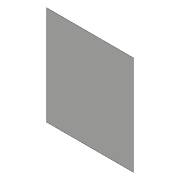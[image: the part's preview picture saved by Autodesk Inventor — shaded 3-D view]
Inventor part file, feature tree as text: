
AUTODESK INVENTOR PART (.ipt)
format: ipt  version: 2017 (Build 210142000, 142)  size: 75,264 bytes
history: native  units: mm
features: extrude x1, sketch x1
ambient origin geometry x8: Origin, YZ Plane, XZ Plane, XY Plane, X Axis, Y Axis, Z Axis, Center Point
bodies: Body1 (feature_tree)
feature tree (2):
  extrude  "Extrusion1"  Depth=838.2mm
  sketch  "Sketch3"  dims[d8=736.6mm d9=838.2mm d10=0.71mm d11=0.0mm]
